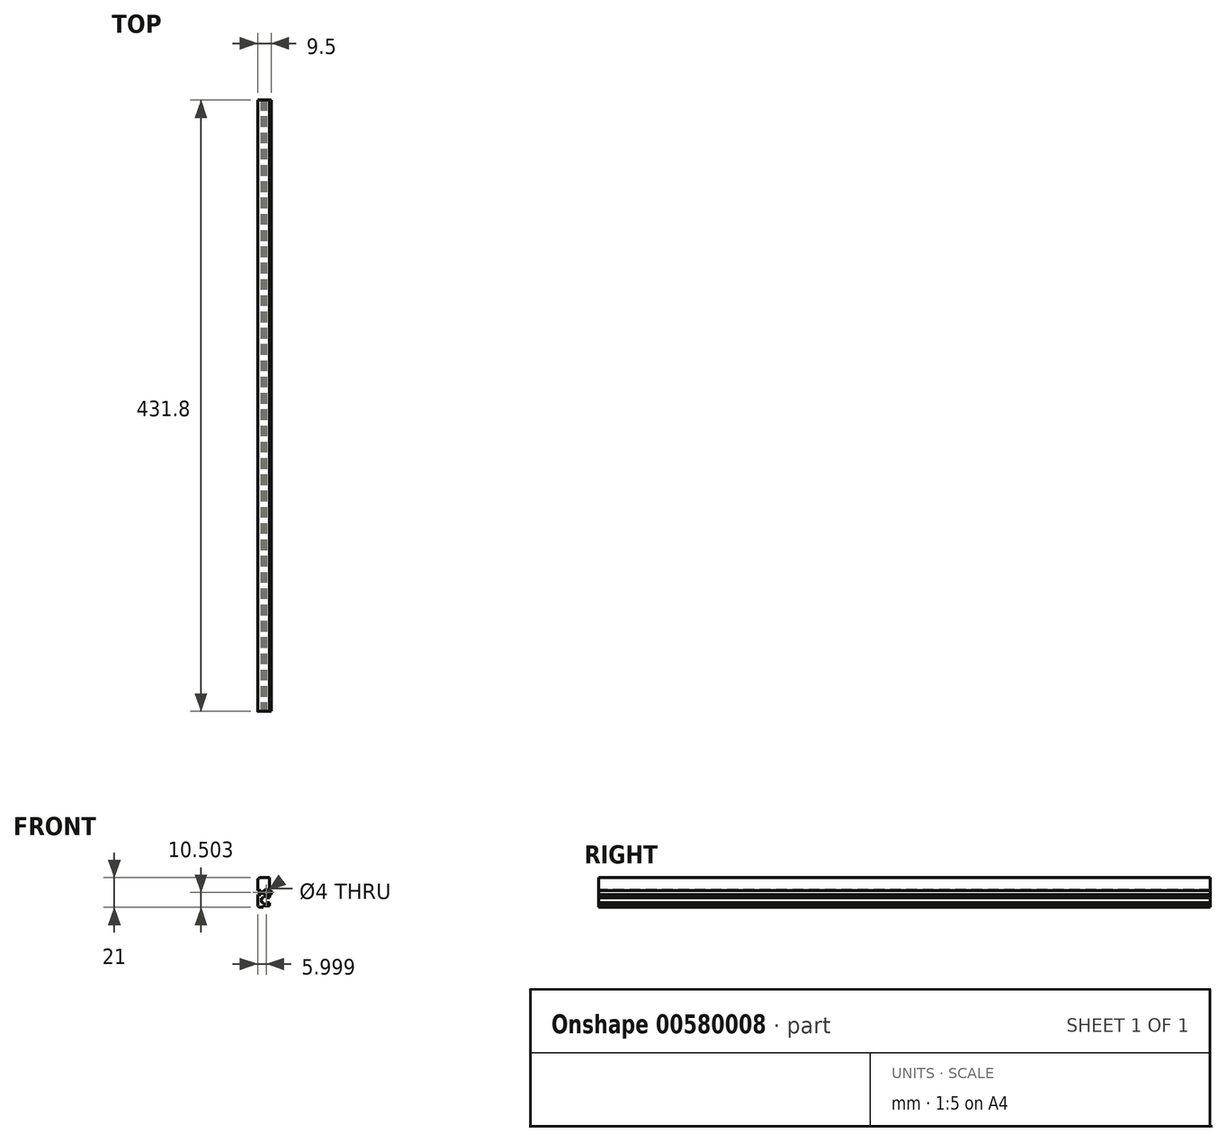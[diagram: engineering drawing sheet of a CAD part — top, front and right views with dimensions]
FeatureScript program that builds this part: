
annotation { "Feature Type Name" : "Feature", "Feature Type Description" : "" }
export const myFeature = defineFeature(function(context is Context, id is Id, definition is map)
    precondition{}
    {
        {
            var Q0;
            Q0=qCreatedBy(makeId("Front.planeOp"),FACE);
            var sketch = newSketch(context, id + "F0", { "sketchPlane" : qUnion([Q0])});
            skLineSegment(sketch, "E0.bottom", {"start": v(-2.52, 3.36) * mm, "end": v(3.98, 3.36) * mm});
            skLineSegment(sketch, "E0.top", {"start": v(-2.52, -17.64) * mm, "end": v(3.98, -17.64) * mm});
            skLineSegment(sketch, "E0.left", {"start": v(-4.52, 1.36) * mm, "end": v(-4.52, -15.64) * mm});
            skLineSegment(sketch, "E0.right", {"start": v(3.98, 3.36) * mm, "end": v(3.98, -17.64) * mm});
            skPoint(sketch, "E1.visualSharp", {"position": v(-4.52, 3.36) * mm});
            skArc(sketch, "E1.filletArc", {"start": v(-2.52, 3.36) * mm, "mid": v(-3.94, 2.78) * mm, "end": v(-4.52, 1.36) * mm});
            skPoint(sketch, "E2.visualSharp", {"position": v(-4.52, -17.64) * mm});
            skArc(sketch, "E2.filletArc", {"start": v(-4.52, -15.64) * mm, "mid": v(-3.94, -17.05) * mm, "end": v(-2.52, -17.64) * mm});
            skLineSegment(sketch, "E3", {"start": v(-4.52, -7.14) * mm, "end": v(3.98, -7.14) * mm, "construction": true});
            skSolve(sketch);
        }
        {
            var Q0;
            Q0 = qSketchRegion(id + "F0", true);
            extrude(context, id + "F1", {"entities" : qUnion([Q0]), "depth" : 431.8 * mm, "offsetDistance" : 25.4 * mm});
        }
        {
            var Q0;
            Q0=makeQuery(id+"F1.opExtrude","CAP_FACE",FACE,{"disambiguationData":[OSD([sQuery(id+"F0.wireOp",EDGE,"E0.bottom"),sQuery(id+"F0.wireOp",EDGE,"E0.top"),sQuery(id+"F0.wireOp",EDGE,"E0.left"),sQuery(id+"F0.wireOp",EDGE,"E0.right"),sQuery(id+"F0.wireOp",EDGE,"E1.filletArc"),sQuery(id+"F0.wireOp",EDGE,"E2.filletArc")])],"isStart":false});
            var sketch = newSketch(context, id + "F2", { "sketchPlane" : qUnion([Q0])});
            skLineSegment(sketch, "E4.0", {"start": v(-4.52, -7.14) * mm, "end": v(3.98, -7.14) * mm, "construction": true});
            skPoint(sketch, "E5", {"position": v(1.48, -7.14) * mm});
            skSolve(sketch);
        }
        {
            var Q0;
            Q0=sQuery(id+"F2.wireOp",VERTEX,"E5");
            var Q1;
            Q1=makeQuery(id+"F1.opExtrude","SWEPT_BODY",BODY,{"disambiguationData":[OSD([sQuery(id+"F0.wireOp",EDGE,"E0.bottom"),sQuery(id+"F0.wireOp",EDGE,"E0.top"),sQuery(id+"F0.wireOp",EDGE,"E0.left"),sQuery(id+"F0.wireOp",EDGE,"E0.right"),sQuery(id+"F0.wireOp",EDGE,"E1.filletArc"),sQuery(id+"F0.wireOp",EDGE,"E2.filletArc")])]});
            hole(context, id + "F3", {"style" : HoleStyle.SIMPLE, "endStyle" : HoleEndStyle.THROUGH, "holeDiameter" : 4 * mm, "majorDiameter" : 6.35 * mm, "isTappedThrough" : true, "tappedDepth" : 12.7 * mm, "tapClearance" : 3, "locations" : qUnion([Q0]), "scope" : qUnion([Q1])});
        }
        {
            var Q0;
            Q0=makeQuery(id+"F1.opExtrude","CAP_FACE",FACE,{"disambiguationData":[OSD([sQuery(id+"F0.wireOp",EDGE,"E0.bottom"),sQuery(id+"F0.wireOp",EDGE,"E0.top"),sQuery(id+"F0.wireOp",EDGE,"E0.left"),sQuery(id+"F0.wireOp",EDGE,"E0.right"),sQuery(id+"F0.wireOp",EDGE,"E1.filletArc"),sQuery(id+"F0.wireOp",EDGE,"E2.filletArc")])],"isStart":false});
            var sketch = newSketch(context, id + "F4", { "sketchPlane" : qUnion([Q0])});
            skLineSegment(sketch, "E6.0", {"start": v(-4.52, -7.14) * mm, "end": v(3.98, -7.14) * mm, "construction": true});
            skLineSegment(sketch, "E7.bottom", {"start": v(3.98, -10.98) * mm, "end": v(-1.02, -10.98) * mm});
            skLineSegment(sketch, "E7.top", {"start": v(3.98, -14.2) * mm, "end": v(-1.02, -14.2) * mm});
            skLineSegment(sketch, "E7.left", {"start": v(3.98, -10.98) * mm, "end": v(3.98, -14.2) * mm});
            skLineSegment(sketch, "E7.right", {"start": v(-2.02, -11.98) * mm, "end": v(-2.02, -13.2) * mm});
            skPoint(sketch, "E8", {"position": v(-2.02, -12.59) * mm});
            skPoint(sketch, "E9.visualSharp", {"position": v(-2.02, -14.2) * mm});
            skArc(sketch, "E9.filletArc", {"start": v(-2.02, -13.2) * mm, "mid": v(-1.73, -13.9) * mm, "end": v(-1.02, -14.2) * mm});
            skPoint(sketch, "E10.visualSharp", {"position": v(-2.02, -10.98) * mm});
            skArc(sketch, "E10.filletArc", {"start": v(-1.02, -10.98) * mm, "mid": v(-1.73, -11.27) * mm, "end": v(-2.02, -11.98) * mm});
            skSolve(sketch);
        }
        {
            var Q0;
            Q0 = qSketchRegion(id + "F4", true);
            extrude(context, id + "F5", {"entities" : qUnion([Q0]), "operationType" : NewBodyOperationType.REMOVE, "oppositeDirection" : true, "depth" : 508 * mm, "offsetDistance" : 25.4 * mm});
        }
        {
            var Q0;
            {var subQ2=sQuery(id+"F4.wireOp",EDGE,"E7.bottom");Q0=makeQuery(id+"F4.imprint","IMPRINT",FACE,{"disambiguationData":[TD([[makeQuery(id+"F4.imprint","IMPRINT",EDGE,{"derivedFrom":subQ2}),-1.0]])]});}
            var sketch = newSketch(context, id + "F6", { "sketchPlane" : qUnion([Q0])});
            skLineSegment(sketch, "E11.bottom", {"start": v(-0.42, -9.94) * mm, "end": v(1.78, -9.94) * mm});
            skLineSegment(sketch, "E11.top", {"start": v(-0.42, -15.24) * mm, "end": v(1.78, -15.24) * mm});
            skLineSegment(sketch, "E11.left", {"start": v(-0.42, -9.94) * mm, "end": v(-0.42, -15.24) * mm});
            skLineSegment(sketch, "E11.right", {"start": v(1.78, -9.94) * mm, "end": v(1.78, -15.24) * mm});
            skPoint(sketch, "E12", {"position": v(-0.42, -12.59) * mm});
            skSolve(sketch);
        }
        {
            var Q0;
            Q0 = qSketchRegion(id + "F6", true);
            extrude(context, id + "F7", {"entities" : qUnion([Q0]), "operationType" : NewBodyOperationType.REMOVE, "oppositeDirection" : true, "depth" : 508 * mm, "offsetDistance" : 25.4 * mm});
        }
        {
            var Q0;
            Q0=makeQuery(id+"F1.opExtrude","SWEPT_FACE",FACE,{"disambiguationData":[OSD([sQuery(id+"F0.wireOp",EDGE,"E0.bottom")])]});
            cPlane(context, id + "F8", {"entities" : qUnion([Q0]), "cplaneType" : CPlaneType.OFFSET, "offset" : 21 * mm / 2, "oppositeDirection" : true, "width" : 152.4 * mm, "height" : 152.4 * mm});
        }
        {
            var Q0;
            {var subQ2=sQuery(id+"F4.wireOp",EDGE,"E7.bottom");Q0=makeQuery(id+"F4.imprint","IMPRINT",FACE,{"disambiguationData":[TD([[makeQuery(id+"F4.imprint","IMPRINT",EDGE,{"derivedFrom":subQ2}),-1.0]])]});}
            var sketch = newSketch(context, id + "F9", { "sketchPlane" : qUnion([Q0])});
            skLineSegment(sketch, "E13.0", {"start": v(3.98, 3.36) * mm, "end": v(3.98, -17.64) * mm, "construction": true});
            skLineSegment(sketch, "E14.bottom", {"start": v(3.98, -5.79) * mm, "end": v(4.98, -5.79) * mm});
            skLineSegment(sketch, "E14.top", {"start": v(3.98, -8.49) * mm, "end": v(4.98, -8.49) * mm});
            skLineSegment(sketch, "E14.left", {"start": v(3.98, -5.79) * mm, "end": v(3.98, -8.49) * mm});
            skLineSegment(sketch, "E14.right", {"start": v(4.98, -5.79) * mm, "end": v(4.98, -8.49) * mm});
            skPoint(sketch, "E15", {"position": v(4.98, -7.14) * mm});
            skSolve(sketch);
        }
        {
            var Q0;
            Q0 = qSketchRegion(id + "F9", true);
            extrude(context, id + "F10", {"entities" : qUnion([Q0]), "operationType" : NewBodyOperationType.ADD, "oppositeDirection" : true, "depth" : 431.8 * mm, "offsetDistance" : 25.4 * mm});
        }
        {
            var Q0;
            {var subQ2=sQuery(id+"F4.wireOp",EDGE,"E7.bottom");Q0=makeQuery(id+"F4.imprint","IMPRINT",FACE,{"disambiguationData":[TD([[makeQuery(id+"F4.imprint","IMPRINT",EDGE,{"derivedFrom":subQ2}),-1.0]])]});}
            var sketch = newSketch(context, id + "F11", { "sketchPlane" : qUnion([Q0])});
            skLineSegment(sketch, "E16.0", {"start": v(-4.52, -7.14) * mm, "end": v(3.98, -7.14) * mm, "construction": true});
            skLineSegment(sketch, "E17.bottom", {"start": v(-2.12, -5.79) * mm, "end": v(-6.92, -5.79) * mm});
            skLineSegment(sketch, "E17.top", {"start": v(-2.12, -8.49) * mm, "end": v(-6.92, -8.49) * mm});
            skLineSegment(sketch, "E17.left", {"start": v(-2.12, -5.79) * mm, "end": v(-2.12, -8.49) * mm});
            skLineSegment(sketch, "E17.right", {"start": v(-6.92, -5.79) * mm, "end": v(-6.92, -8.49) * mm});
            skPoint(sketch, "E17.middle", {"position": v(-4.52, -7.14) * mm});
            skSolve(sketch);
        }
        {
            var Q0;
            Q0 = qSketchRegion(id + "F11", true);
            extrude(context, id + "F12", {"entities" : qUnion([Q0]), "operationType" : NewBodyOperationType.REMOVE, "oppositeDirection" : true, "depth" : 431.8 * mm, "offsetDistance" : 25.4 * mm});
        }
        {
            var Q0;
            {var subQ2=sQuery(id+"F4.wireOp",EDGE,"E7.bottom");Q0=makeQuery(id+"F4.imprint","IMPRINT",FACE,{"disambiguationData":[TD([[makeQuery(id+"F4.imprint","IMPRINT",EDGE,{"derivedFrom":subQ2}),-1.0]])]});}
            var sketch = newSketch(context, id + "F13", { "sketchPlane" : qUnion([Q0])});
            skLineSegment(sketch, "E18.0", {"start": v(-2.52, -17.64) * mm, "end": v(3.98, -17.64) * mm, "construction": true});
            skLineSegment(sketch, "E19.0", {"start": v(3.98, 3.36) * mm, "end": v(3.98, -17.64) * mm, "construction": true});
            skLineSegment(sketch, "E20", {"start": v(3.98, -17.64) * mm, "end": v(3.98, -16.46) * mm});
            skLineSegment(sketch, "E21", {"start": v(3.98, -16.46) * mm, "end": v(0.91, -16.46) * mm});
            skLineSegment(sketch, "E22", {"start": v(0.91, -16.46) * mm, "end": v(0.3, -16.2) * mm});
            skLineSegment(sketch, "E23", {"start": v(0.3, -16.2) * mm, "end": v(-0.72, -16.2) * mm});
            skLineSegment(sketch, "E24", {"start": v(-0.72, -16.2) * mm, "end": v(-0.72, -17.64) * mm});
            skLineSegment(sketch, "E25", {"start": v(-0.72, -17.64) * mm, "end": v(3.98, -17.64) * mm});
            skSolve(sketch);
        }
        {
            var Q0;
            Q0 = qSketchRegion(id + "F13", true);
            extrude(context, id + "F14", {"entities" : qUnion([Q0]), "operationType" : NewBodyOperationType.REMOVE, "oppositeDirection" : true, "depth" : 431.8 * mm, "offsetDistance" : 25.4 * mm});
        }
    });
